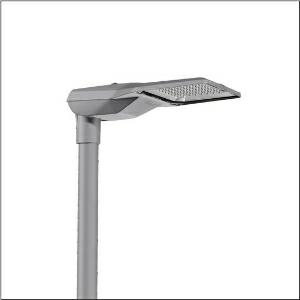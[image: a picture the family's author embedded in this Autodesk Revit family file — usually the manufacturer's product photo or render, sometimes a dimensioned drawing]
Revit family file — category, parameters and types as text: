
# Revit family: streetlight_sl_21_midi___st1_5a_5xe3p33s08lb_eae5
name_source: partatom
category: Lighting Fixtures
units: mm (PartAtom-declared; Revit-internal decimal feet)

## family parameters
Cut with Voids When Loaded = No
Host = Face
Light Source = No
Part Type = Normal
Room Calculation Point = No
Round Connector Dimension = Use Diameter
Shared = No

## types (1)
- --- (1 x LED, 14100 lm, 99.6 W, 3000K)
    Apparent Load = 100 VA
    CIE Flux Codes = 22 53 95 100 100
    Color Rendering = 70
    Color Temperature = 3000K
    Default Elevation = 1800 mm
    Description = Streetlight SL 21 midi, mast luminaire, primary light control with lens, of PMMA, primary optical cover: cover, of toughened safety glass, transparent, light distribution: ST1.5a, light emission: direct distribution, primary light characteristic: asymmetric, installation type: side-entry, post-top, LED, High Power LED, rated luminous flux: 14.100lm, luminous efficacy: 142lm/W, light colour: 730, colour temperature: 3000K, control gear: D4i, control: overheat protection, constant luminous flux control, time-dependent luminous flux control, flexible luminous flux parameterisation, pre-setting: logarithmic dimming characteristic, mains connection: 230..240V, AC, 50/60Hz, start of lifetime: 100W, end of service life: 102W, reduction: 46W, luminaire housing, of diecast aluminium, powder-coated, Siteco® metallic grey (DB 702S), corrosivity category C5 mid according to DIN EN ISO 12944, please order mast flange separately, inclination adjustable: 0°, 5°, 10°, 15°, sealing non-destructively replaceable, multi-level sealing system, length: 644mm, width: 335mm, height: 110mm, mast flange for spigot size: 42mm (side-entry): 5XC10008XM4, 60/48mm (side-entry/post-top): 5XC10108XM2, 76/60mm (side-entry/post-top): 5XC10108XM1, mounting height: 4..8m, Smart Interface above, protection rating (complete): IP66, insulation class (complete): insulation class II (safety insulation), certification: CE, ENEC, ENEC+, VDE, impact resistance: IK10, permissible operating ambient temperature for outdoor applications: -40..+50°C, standard-compliant lighting for roads and squares, packaging unit: 1 piece

Light Distribution: ST1.5a
    Height = 111 mm
    Lamp = 1 x LED
    Lamp Light Flux = 14100 lm
    Lamp Power = 99.6 W
    Lamp count = 1
    Length = 644 mm
    Luminous efficacy = 142 lm/W
    Manufacturer = Siteco
    ModVariant = No
    Model = 5XE3P33S08LB
    Number of Poles = 1
    OnlyDefault = Yes
    Power Factor = 1
    Product Name = Streetlight SL 21 midi | ST1.5a
    Product group = mast luminaire | pylon top
    ProductGroupID = 6100
    Protection Class = Protection class II
    Protection Degree = IP 66
    RLX_Detail_Level = 1
    RLX_Emergency_Light_Flux = 0 lm
    RLX_Emergency_Type = 0
    RLX_Emergency_Type_DB = No
    RlxData = <blob elided: 30313 chars, md5=f8919b25>
    Socket = socket
    Standby Power = 0 W
    System Light Flux = 14100 lm
    System Power = 100 W
    Type Comments = factory setting: luminous flux: 100 % | dim-lin: 254 | 1020 mA
    Type Image = l_1004302.jpg
    URL = http://relux.com
    VarID = @adj_012897
    Voltage = 0 V
    Weight = 0.00 kg
    Width = 336 mm

## geometry (parser evidence)
native form markers: Blend x4, Sweep x8
no freeform markers — native parametric forms only
